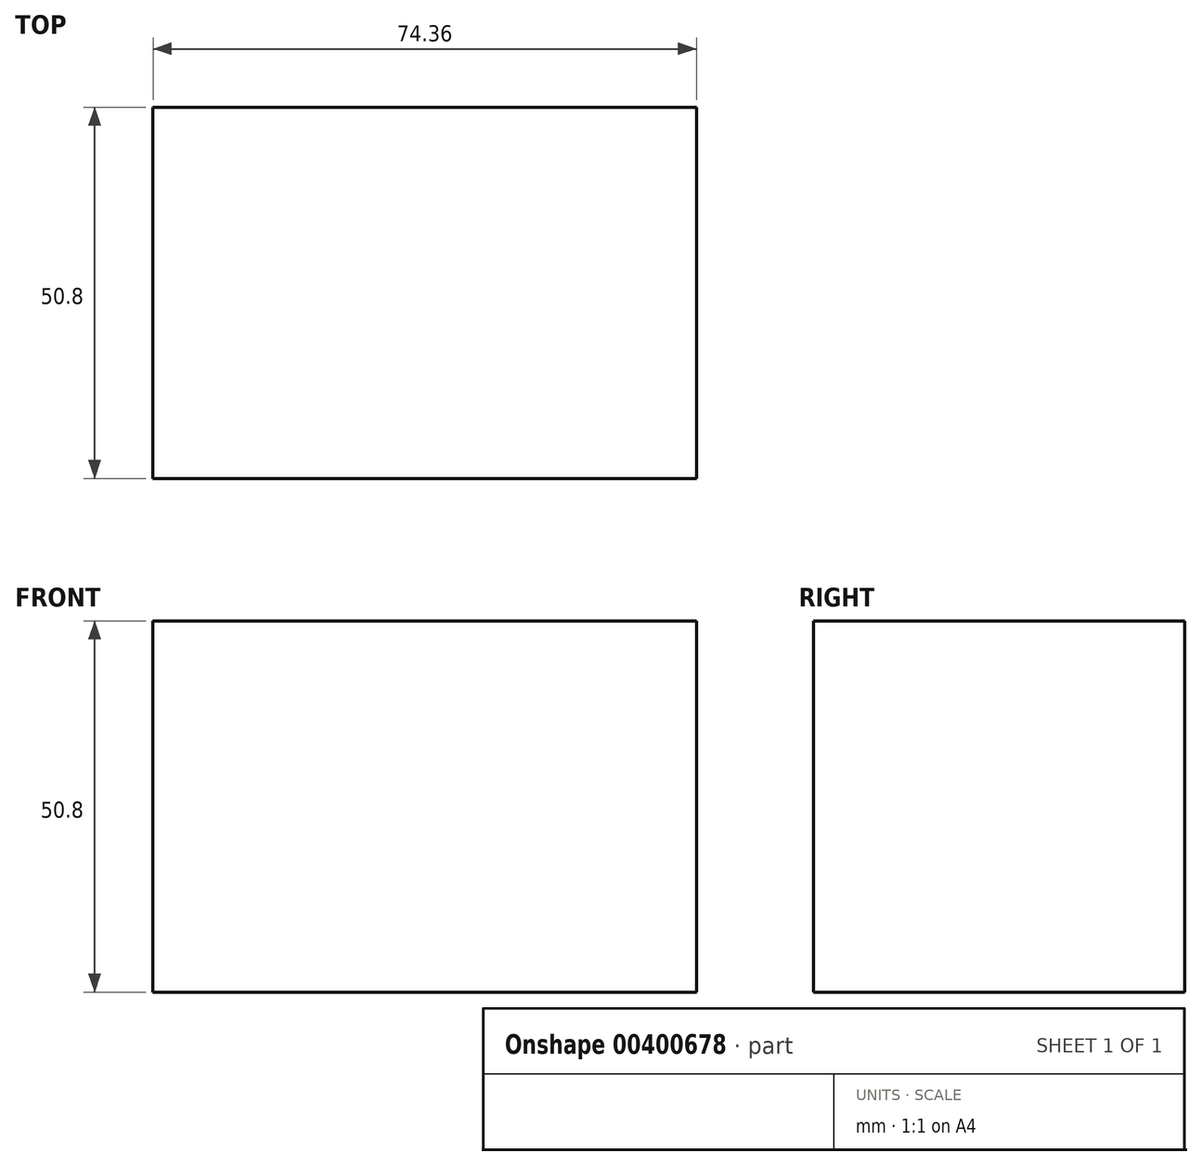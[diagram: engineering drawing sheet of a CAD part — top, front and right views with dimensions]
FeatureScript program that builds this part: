
annotation { "Feature Type Name" : "Feature", "Feature Type Description" : "" }
export const myFeature = defineFeature(function(context is Context, id is Id, definition is map)
    precondition{}
    {
        {
            var Q0;
            Q0=qCreatedBy(makeId("Top.planeOp"),FACE);
            var sketch = newSketch(context, id + "F0", { "sketchPlane" : qUnion([Q0])});
            skLineSegment(sketch, "E0.bottom", {"start": v(-35.5, 35.68) * mm, "end": v(38.86, 35.68) * mm});
            skLineSegment(sketch, "E0.top", {"start": v(-35.5, -30.89) * mm, "end": v(38.86, -30.89) * mm});
            skLineSegment(sketch, "E0.left", {"start": v(-35.5, 35.68) * mm, "end": v(-35.5, -30.89) * mm});
            skLineSegment(sketch, "E0.right", {"start": v(38.86, 35.68) * mm, "end": v(38.86, -30.89) * mm});
            skSolve(sketch);
        }
        {
            var Q0;
            Q0=sQuery(id+"F0.wireOp",EDGE,"E0.top");
            extrude(context, id + "F1", {"bodyType" : ToolBodyType.SURFACE, "surfaceEntities" : qUnion([Q0]), "depth" : 50.8 * mm});
        }
        {
            var Q0;
            Q0=makeQuery(id+"F1.opExtrude","SWEPT_FACE",FACE,{"disambiguationData":[OSD([sQuery(id+"F0.wireOp",EDGE,"E0.top")])]});
            extrude(context, id + "F2", {"entities" : qUnion([Q0]), "depth" : 50.8 * mm});
        }
        {
            var Q0;
            {var subQ0=sQuery(id+"F0.wireOp",EDGE,"E0.top");Q0=makeQuery(id+"F2.opExtrude","SWEPT_FACE",FACE,{"disambiguationData":[OSD([subQ0]),TDD([makeQuery(id+"F1.opExtrude","CAP_EDGE",EDGE,{"disambiguationData":[OSD([subQ0])],"isStart":false})])]});}
            var sketch = newSketch(context, id + "F3", { "sketchPlane" : qUnion([Q0])});
            skCircle(sketch, "E1", {"center": v(0, -52.53) * mm, "radius": 17.95 * mm});
            skSolve(sketch);
        }
        {
            var Q0;
            Q0=makeQuery(id+"F3.imprint","IMPRINT",FACE,{"disambiguationData":[TD([[makeQuery(id+"F3.imprint","IMPRINT",EDGE,{"derivedFrom":sQuery(id+"F3.wireOp",EDGE,"E1")}),1.0]])]});
            extrude(context, id + "F4", {"entities" : qUnion([Q0]), "operationType" : NewBodyOperationType.ADD, "depth" : -50.8 * mm});
        }
    });
